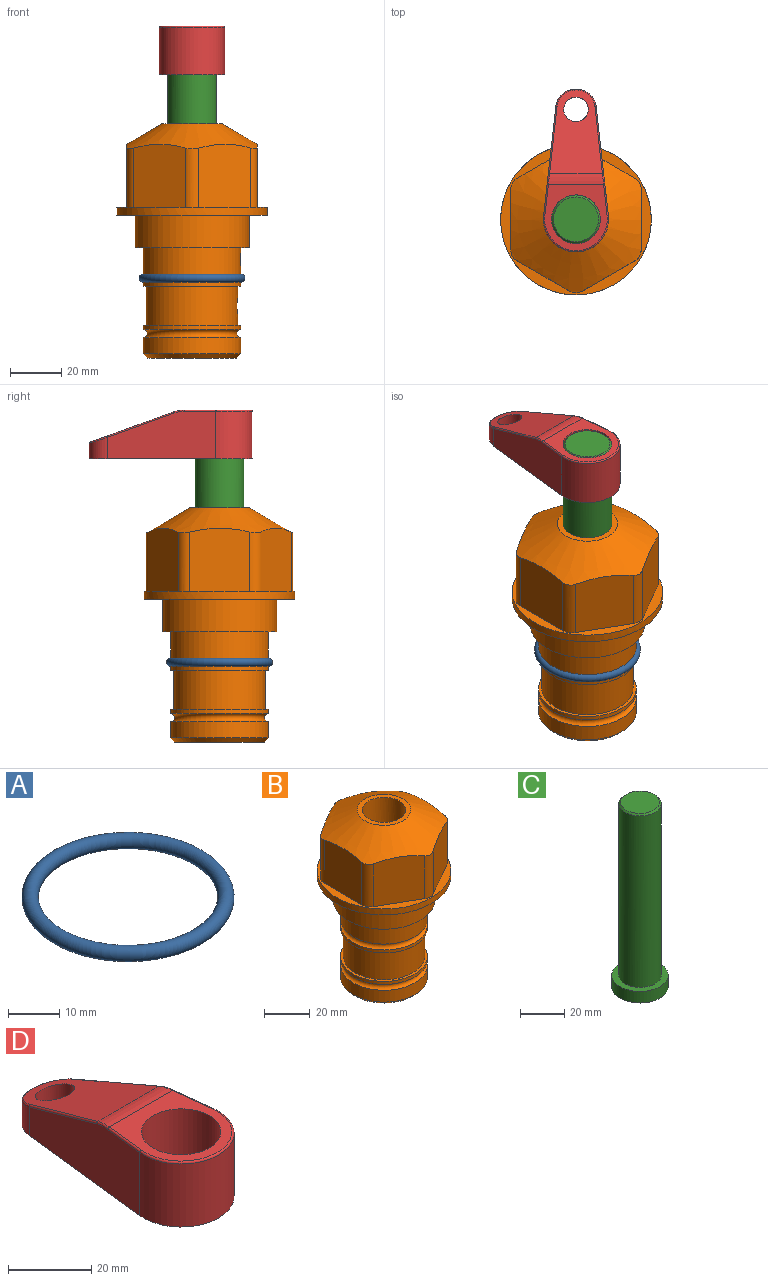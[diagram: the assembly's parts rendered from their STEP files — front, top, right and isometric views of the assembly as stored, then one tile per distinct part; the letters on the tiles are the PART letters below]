
ASSEMBLY  parts=4 mates=2
PART A: 1 faces, bbox 44.7x44.7x3.2 mm
  f0: torus R=19.05mm, axis (0,0,1), area 1193.9mm2
PART B: 36 faces, bbox 58.7x58.7x91.2 mm
  f0: cylinder r=17.78mm len=35.56mm, axis (0,0,1), area 1670.8mm2, adj f23,f24,f31
  f1: cylinder r=19.05mm len=38.1mm, axis (0,0,1), area 1191.9mm2, adj f26,f27,f30
  f2: plane 58.66x58.66mm, normal (0,0,-1), area 1150.6mm2, adj f3,f28
  f3: cylinder r=29.33mm len=58.66mm, axis (0,0,-1), area 585.1mm2, adj f2,f4
  f4: plane 58.66x58.66mm, normal (0,0,1), area 475.9mm2, adj f3,f5,f6,f7,f8,f9,f10,f11
  f5: plane 24.5x20.32mm, normal (0.5,-0.87,0), area 562.8mm2, adj f4,f15,f16,f17
  f6: plane 24.5x20.32mm, normal (-0.5,-0.87,0), area 562.8mm2, adj f4,f14,f15,f17
  f7: plane 24.5x23.48mm, normal (-1,0,0), area 562.8mm2, adj f4,f13,f14,f17
  f8: plane 24.5x20.32mm, normal (-0.5,0.87,0), area 562.8mm2, adj f4,f12,f13,f17
  f9: plane 24.5x20.32mm, normal (0.5,0.87,0), area 562.8mm2, adj f4,f11,f12,f17
  f10: plane 24.5x23.48mm, normal (1,0,0), area 562.8mm2, adj f4,f11,f16,f17
  f11: cylinder r=5.08mm len=23.01mm, axis (0,0,-1), area 121.2mm2, adj f4,f9,f10,f17
  f12: cylinder r=5.08mm len=23.01mm, axis (0,0,-1), area 121.2mm2, adj f4,f8,f9,f17
  f13: cylinder r=5.08mm len=23.01mm, axis (0,0,-1), area 121.2mm2, adj f4,f7,f8,f17
  f14: cylinder r=5.08mm len=23.01mm, axis (0,0,-1), area 121.2mm2, adj f4,f6,f7,f17
  f15: cylinder r=5.08mm len=23.01mm, axis (0,0,-1), area 121.2mm2, adj f4,f5,f6,f17
  f16: cylinder r=5.08mm len=23.01mm, axis (0,0,-1), area 121.2mm2, adj f4,f5,f10,f17
  f17: cone r=11.73mm half-angle=60deg, axis (0,0,-1), area 2071.8mm2, adj f5,f6,f7,f8,f9,f10,f11,f12
  f18: plane 23.46x23.46mm, normal (0,0,1), area 147.4mm2, adj f17,f35
  f19: plane 34.93x34.93mm, normal (0,0,-1), area 958mm2, adj f29
  f20: cylinder r=19.05mm len=38.1mm, axis (0,0,1), area 760.1mm2, adj f21,f29
  f21: torus R=19.05mm, axis (0,0,1), area 565.3mm2, adj f20,f22
  f22: cylinder r=19.05mm len=38.1mm, axis (0,0,1), area 190mm2, adj f21,f23
  f23: plane 38.1x38.1mm, normal (0,0,1), area 146.9mm2, adj f0,f22
  f24: plane 38.1x38.1mm, normal (0,0,-1), area 146.9mm2, adj f0,f25
  f25: cylinder r=19.05mm len=38.1mm, axis (0,0,1), area 190mm2, adj f24,f26
  f26: torus R=19.05mm, axis (0,0,1), area 565.3mm2, adj f1,f25
  f27: plane 44.45x44.45mm, normal (0,0,-1), area 411.7mm2, adj f1,f28
  f28: cylinder r=22.23mm len=44.45mm, axis (0,0,1), area 1773.5mm2, adj f2,f27
  f29: cone r=19.05mm half-angle=45deg, axis (0,0,1), area 257.5mm2, adj f19,f20
  f30: cylinder r=3.17mm len=6.75mm, axis (-1,0,0), area 128mm2, adj f1,f33
  f31: cylinder r=3.17mm len=6.35mm, axis (-1,0,0), area 102.5mm2, adj f0,f33
  f32: plane 25.4x25.4mm, normal (0,0,1), area 506.7mm2, adj f33
  f33: cylinder r=12.7mm len=66.42mm, axis (0,0,-1), area 5236.2mm2, adj f30,f31,f32,f34
  f34: cone r=9.53mm half-angle=30deg, axis (0,0,-1), area 443.4mm2, adj f33,f35
  f35: cylinder r=9.53mm len=19.05mm, axis (0,0,-1), area 849mm2, adj f18,f34
PART C: 6 faces, bbox 25.4x25.4x101.6 mm
  f0: plane 17.46x17.46mm, normal (0,0,1), area 239.5mm2, adj f5
  f1: plane 25.4x25.4mm, normal (0,0,-1), area 506.7mm2, adj f2
  f2: cylinder r=12.7mm len=25.4mm, axis (0,0,1), area 506.7mm2, adj f1,f3
  f3: plane 25.4x25.4mm, normal (0,0,1), area 221.7mm2, adj f2,f4
  f4: cylinder r=9.53mm len=94.46mm, axis (0,0,1), area 5653mm2, adj f3,f5
  f5: cone r=8.73mm half-angle=45deg, axis (0,0,-1), area 64.4mm2, adj f0,f4
PART D: 44 faces, bbox 27.5x64.5x19.1 mm
  f0: plane 2.3x0.95mm, normal (0,0,-1), area 1mm2, adj f25,f30,f34
  f1: plane 63.5x25.4mm, normal (0,0,-1), area 561.7mm2, adj f2,f3,f4,f5,f6,f7,f19,f20
  f2: cylinder r=12.7mm len=25.4mm, axis (0,0,-1), area 792.2mm2, adj f1,f3,f5,f13
  f3: plane 42.33x18.54mm, normal (0.99,0.11,0), area 647mm2, adj f1,f2,f4,f11,f12,f14
  f4: cylinder r=7.94mm len=15.78mm, axis (0,0,-1), area 158.6mm2, adj f1,f3,f5,f16
  f5: plane 42.33x18.54mm, normal (-0.99,0.11,0), area 647mm2, adj f1,f2,f4,f15,f17,f18
  f6: cylinder r=9.53mm len=19.05mm, axis (0,0,-1), area 1140.1mm2, adj f1,f8
  f7: cylinder r=4.76mm len=10.98mm, axis (0,0,-1), area 276.1mm2, adj f1,f9
  f8: plane 25.83x24.38mm, normal (0,0,1), area 262.2mm2, adj f6,f10,f11,f13,f15
  f9: plane 32.49x20.55mm, normal (0,0.34,0.94), area 489.9mm2, adj f7,f10,f14,f16,f18
  f10: cylinder r=12.7mm len=21.49mm, axis (-1,0,0), area 93.2mm2, adj f8,f9,f12,f17
  f11: cylinder r=0.51mm len=12.34mm, axis (0.11,-0.99,0), area 9.9mm2, adj f3,f8,f12,f13
  f12: bspline ~7.62x1.64mm, area 3.5mm2, adj f3,f10,f11,f14
  f13: torus R=12.19mm, axis (0,0,1), area 33.6mm2, adj f2,f8,f11,f15
  f14: cylinder r=0.51mm len=26.01mm, axis (0.1,-0.93,0.34), area 21.6mm2, adj f3,f9,f12,f16
  f15: cylinder r=0.51mm len=12.34mm, axis (0.11,0.99,0), area 9.9mm2, adj f5,f8,f13,f17
  f16: bspline ~15.78x7.05mm, area 15.7mm2, adj f4,f9,f14,f18
  f17: bspline ~7.62x1.64mm, area 3.5mm2, adj f5,f10,f15,f18
  f18: cylinder r=0.51mm len=26.01mm, axis (0.1,0.93,-0.34), area 21.6mm2, adj f5,f9,f16,f17
  f19: plane 21.6x14.29mm, normal (-0.99,-0.11,0), area 242.6mm2, adj f1,f26,f28,f34,f36,f38
  f20: plane 21.6x14.29mm, normal (0.99,-0.11,0), area 242.6mm2, adj f1,f27,f29,f37,f39,f41
  f21: cylinder r=12.7mm len=14.29mm, axis (0,0,-1), area 173.2mm2, adj f1,f26,f27,f30,f31,f33
  f22: cylinder r=7.94mm len=7.63mm, axis (0,0,-1), area 53.8mm2, adj f1,f28,f29,f42
  f23: plane 2.3x0.95mm, normal (0,0,-1), area 1mm2, adj f25,f33,f37
  f24: plane 17.94x12.32mm, normal (0,-0.34,-0.94), area 191.2mm2, adj f25,f38,f41,f42
  f25: cylinder r=9.53mm len=12.93mm, axis (-1,0,0), area 37.5mm2, adj f0,f23,f24,f31,f36,f39
  f26: cylinder r=1.59mm len=14.29mm, axis (0,0,-1), area 49mm2, adj f1,f19,f21,f32
  f27: cylinder r=1.59mm len=14.29mm, axis (0,0,-1), area 49mm2, adj f1,f20,f21,f35
  f28: cylinder r=1.59mm len=7.28mm, axis (0,0,-1), area 22.1mm2, adj f1,f19,f22,f40
  f29: cylinder r=1.59mm len=7.28mm, axis (0,0,-1), area 22.1mm2, adj f1,f20,f22,f43
  f30: torus R=14.29mm, axis (0,0,1), area 5.8mm2, adj f0,f21,f31,f32
  f31: bspline ~11.06x2.73mm, area 20.8mm2, adj f21,f25,f30,f33
  f32: sphere r=1.59mm, area 5.4mm2, adj f26,f30,f34
  f33: torus R=14.29mm, axis (0,0,1), area 5.8mm2, adj f21,f23,f31,f35
  f34: cylinder r=1.59mm len=1.68mm, axis (-0.11,0.99,0), area 2.4mm2, adj f0,f19,f32,f36
  f35: sphere r=1.59mm, area 5.4mm2, adj f27,f33,f37
  f36: bspline ~5.82x2.33mm, area 7.7mm2, adj f19,f25,f34,f38
  f37: cylinder r=1.59mm len=1.68mm, axis (0.11,0.99,0), area 2.4mm2, adj f20,f23,f35,f39
  f38: cylinder r=1.59mm len=18.33mm, axis (0.1,-0.93,0.34), area 46.7mm2, adj f19,f24,f36,f40
  f39: bspline ~5.82x2.33mm, area 7.7mm2, adj f20,f25,f37,f41
  f40: sphere r=1.59mm, area 3.6mm2, adj f28,f38,f42
  f41: cylinder r=1.59mm len=18.33mm, axis (0.1,0.93,-0.34), area 46.7mm2, adj f20,f24,f39,f43
  f42: bspline ~8.31x1.84mm, area 15.3mm2, adj f22,f24,f40,f43
  f43: sphere r=1.59mm, area 3.6mm2, adj f29,f41,f42
PLACE A at identity
PLACE B at identity fixed
PLACE C t=(0,0,0.08)mm
PLACE D t=(0,0,54.69)mm
MATE cylindrical C.f2 <-> B.f0  axis (0,0,1) through (0,0,25.72)mm
MATE fastened D.f2 <-> C.f2  axis (0,0,-1) through (0,0,73.74)mm
